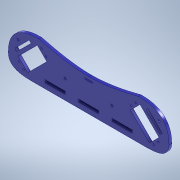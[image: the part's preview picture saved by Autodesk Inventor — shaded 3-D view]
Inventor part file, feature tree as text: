
AUTODESK INVENTOR PART (.ipt)
format: ipt  version: 2020.3 (Build 243373000, 373)  size: 300,544 bytes
history: native  units: mm
features: extrude x6, sketch x6, projected_geometry x3, move_body x2, direct_edit x1
ambient origin geometry x8: Origin, YZ Plane, XZ Plane, XY Plane, X Axis, Y Axis, Z Axis, Center Point
bodies: Solid1 (feature_tree)
feature tree (18):
  extrude  "Extrusion1"  TaperAngle=0.0deg  [1 undecoded]
  extrude  "Extrusion2"  TaperAngle=0.0deg  [1 undecoded]
  extrude  "Extrusion3"  TaperAngle=0.0deg  [1 undecoded]
  extrude  "Extrusion4"  Depth=5.0mm
  extrude  "Extrusion5"  [1 undecoded]
  direct_edit  "Direct Edit1"
  extrude  "Extrusion6"  [1 undecoded]
  sketch  "Sketch1"  dims[d2=4.0mm d3=0.0mm d8=0.0mm d9=0.0mm]
  sketch  "Sketch2"  dims[d10=0.0mm d11=0.0mm d19=0.0mm d20=0.0mm]
  sketch  "Sketch3"  dims[d23=10.0mm d24=0.0mm d25=0.0mm d26=-15.0mm d27=0.0mm]
  projected_geometry  "Projected Loop1"
  sketch  "Sketch4"  dims[d28=0.0mm d29=-15.0mm d30=0.0mm d31=5.0mm d32=2.0mm]
  sketch  "Sketch5"  dims[d33=0.0mm d34=0.0mm]
  projected_geometry  "Projected Loop2"
  sketch  "Sketch6"
  projected_geometry  "Projected Loop3"
  move_body  "Move1"
  move_body  "Move2"
note: 5 required parameter values undecoded (feature->parameter linkage not recoverable at this tier; creation-order binding heuristic only, values carry confidence <= 0.55)
